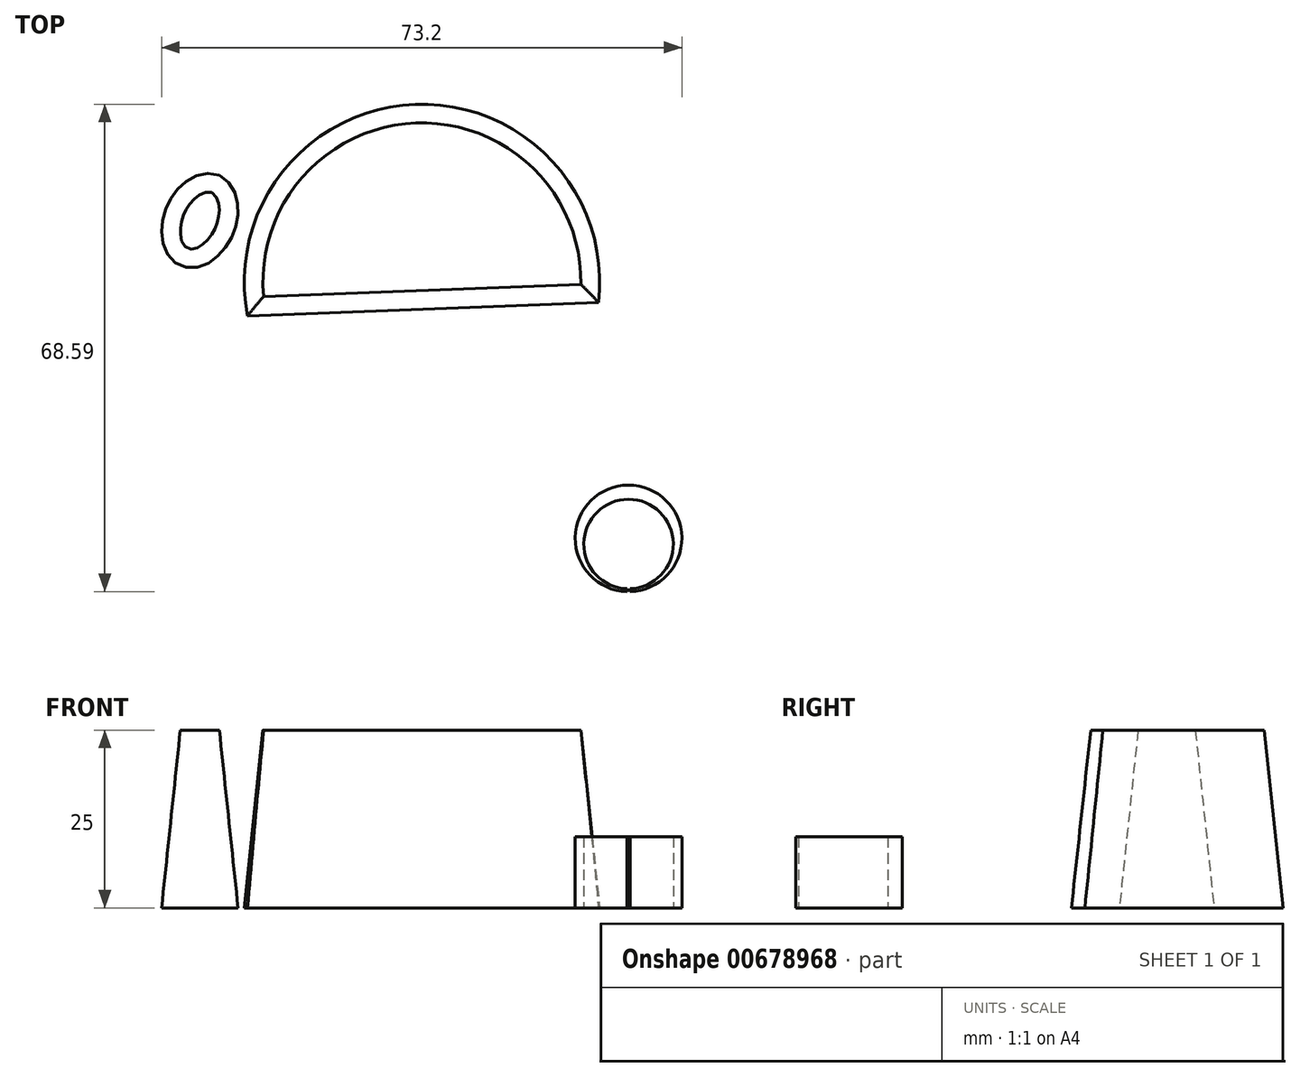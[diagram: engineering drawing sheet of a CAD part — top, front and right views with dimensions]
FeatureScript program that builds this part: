
annotation { "Feature Type Name" : "Feature", "Feature Type Description" : "" }
export const myFeature = defineFeature(function(context is Context, id is Id, definition is map)
    precondition{}
    {
        {
            var Q0;
            Q0=qCreatedBy(makeId("Top.planeOp"),FACE);
            var sketch = newSketch(context, id + "F0", { "sketchPlane" : qUnion([Q0])});
            skLineSegment(sketch, "E0", {"start": v(-0.19, -4.08) * mm, "end": v(-0.19, -4.08) * mm});
            skLineSegment(sketch, "E1", {"start": v(0, -3.54) * mm, "end": v(0, -3.54) * mm});
            skArc(sketch, "E2", {"start": v(0.21, -7.5) * mm, "mid": v(0, 7.5) * mm, "end": v(-0.21, -7.5) * mm});
            skLineSegment(sketch, "E3", {"start": v(0, 9.87) * mm, "end": v(0, -11.91) * mm, "construction": true});
            skArc(sketch, "E4", {"start": v(-0.2, -7.1) * mm, "mid": v(0, 5.5) * mm, "end": v(0.2, -7.1) * mm});
            skPoint(sketch, "E4.first.point", {"position": v(0, -7.5) * mm});
            skPoint(sketch, "E4.second.point", {"position": v(0, 5.5) * mm});
            skPoint(sketch, "E5", {"position": v(0, 7.5) * mm});
            skPoint(sketch, "E6", {"position": v(0, -7.1) * mm});
            skLineSegment(sketch, "E7", {"start": v(-0.2, -7.1) * mm, "end": v(-0.21, -7.5) * mm});
            skLineSegment(sketch, "E8", {"start": v(0.2, -7.1) * mm, "end": v(0.21, -7.5) * mm});
            skSolve(sketch);
        }
        {
            var Q0;
            Q0 = qSketchRegion(id + "F0", true);
            extrude(context, id + "F1", {"entities" : qUnion([Q0]), "depth" : 10 * mm, "offsetDistance" : 25 * mm});
        }
        {
            var Q0;
            Q0=qCreatedBy(makeId("Top.planeOp"),FACE);
            var sketch = newSketch(context, id + "F2", { "sketchPlane" : qUnion([Q0])});
            skEllipse(sketch, "E9", {"center": v(-60.32, 44.72) * mm, "majorRadius": 6.92 * mm, "minorRadius": 5.04 * mm, "majorAxis": v(-0.4, -0.92)});
            skArc(sketch, "E10", {"start": v(-4.23, 33.2) * mm, "mid": v(-30.02, 61.07) * mm, "end": v(-53.6, 31.32) * mm});
            skLineSegment(sketch, "E11", {"start": v(-4.23, 33.2) * mm, "end": v(-53.6, 31.32) * mm});
            skPoint(sketch, "E12.orphan", {"position": v(70.93, 36.09) * mm});
            skSolve(sketch);
        }
        {
            var Q0;
            Q0 = qSketchRegion(id + "F2", true);
            extrude(context, id + "F3", {"entities" : qUnion([Q0]), "depth" : 25 * mm, "offsetDistance" : 25 * mm, "hasDraft" : true, "draftAngle" : 6 * degree, "draftPullDirection" : true});
        }
    });
